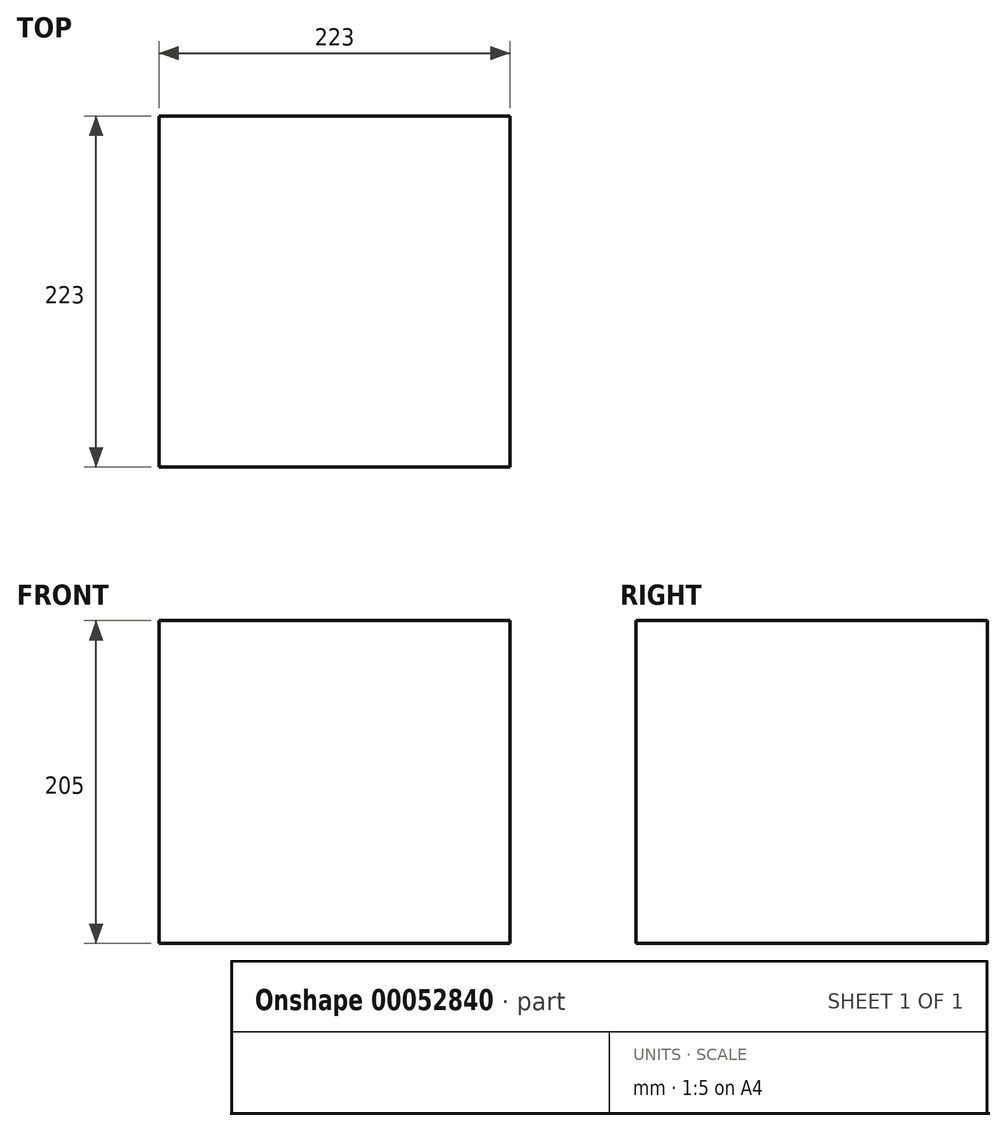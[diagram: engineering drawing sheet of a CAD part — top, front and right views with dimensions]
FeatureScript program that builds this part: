
annotation { "Feature Type Name" : "Feature", "Feature Type Description" : "" }
export const myFeature = defineFeature(function(context is Context, id is Id, definition is map)
    precondition{}
    {
        {
            var Q0;
            Q0=qCreatedBy(makeId("Top.planeOp"),FACE);
            var sketch = newSketch(context, id + "F0", { "sketchPlane" : qUnion([Q0])});
            skLineSegment(sketch, "E0.bottom", {"start": v(-168.98, 55.53) * mm, "end": v(54.02, 55.53) * mm});
            skLineSegment(sketch, "E0.top", {"start": v(-168.98, -167.47) * mm, "end": v(54.02, -167.47) * mm});
            skLineSegment(sketch, "E0.left", {"start": v(-168.98, 55.53) * mm, "end": v(-168.98, -167.47) * mm});
            skLineSegment(sketch, "E0.right", {"start": v(54.02, 55.53) * mm, "end": v(54.02, -167.47) * mm});
            skSolve(sketch);
        }
        {
            var Q0;
            Q0=makeQuery(id+"F0.imprint","IMPRINT",FACE,{"disambiguationData":[TD([[makeQuery(id+"F0.imprint","IMPRINT",EDGE,{"derivedFrom":sQuery(id+"F0.wireOp",EDGE,"E0.bottom")}),-1.0]])]});
            var Q1;
            Q1=sQuery(id+"F0.wireOp",EDGE,"E0.bottom");
            var Q2;
            Q2=sQuery(id+"F0.wireOp",EDGE,"E0.top");
            var Q3;
            Q3=sQuery(id+"F0.wireOp",EDGE,"E0.left");
            var Q4;
            Q4=sQuery(id+"F0.wireOp",EDGE,"E0.right");
            extrude(context, id + "F1", {"entities" : qUnion([Q0]), "surfaceEntities" : qUnion([Q1, Q2, Q3, Q4]), "depth" : 205 * mm});
        }
    });
